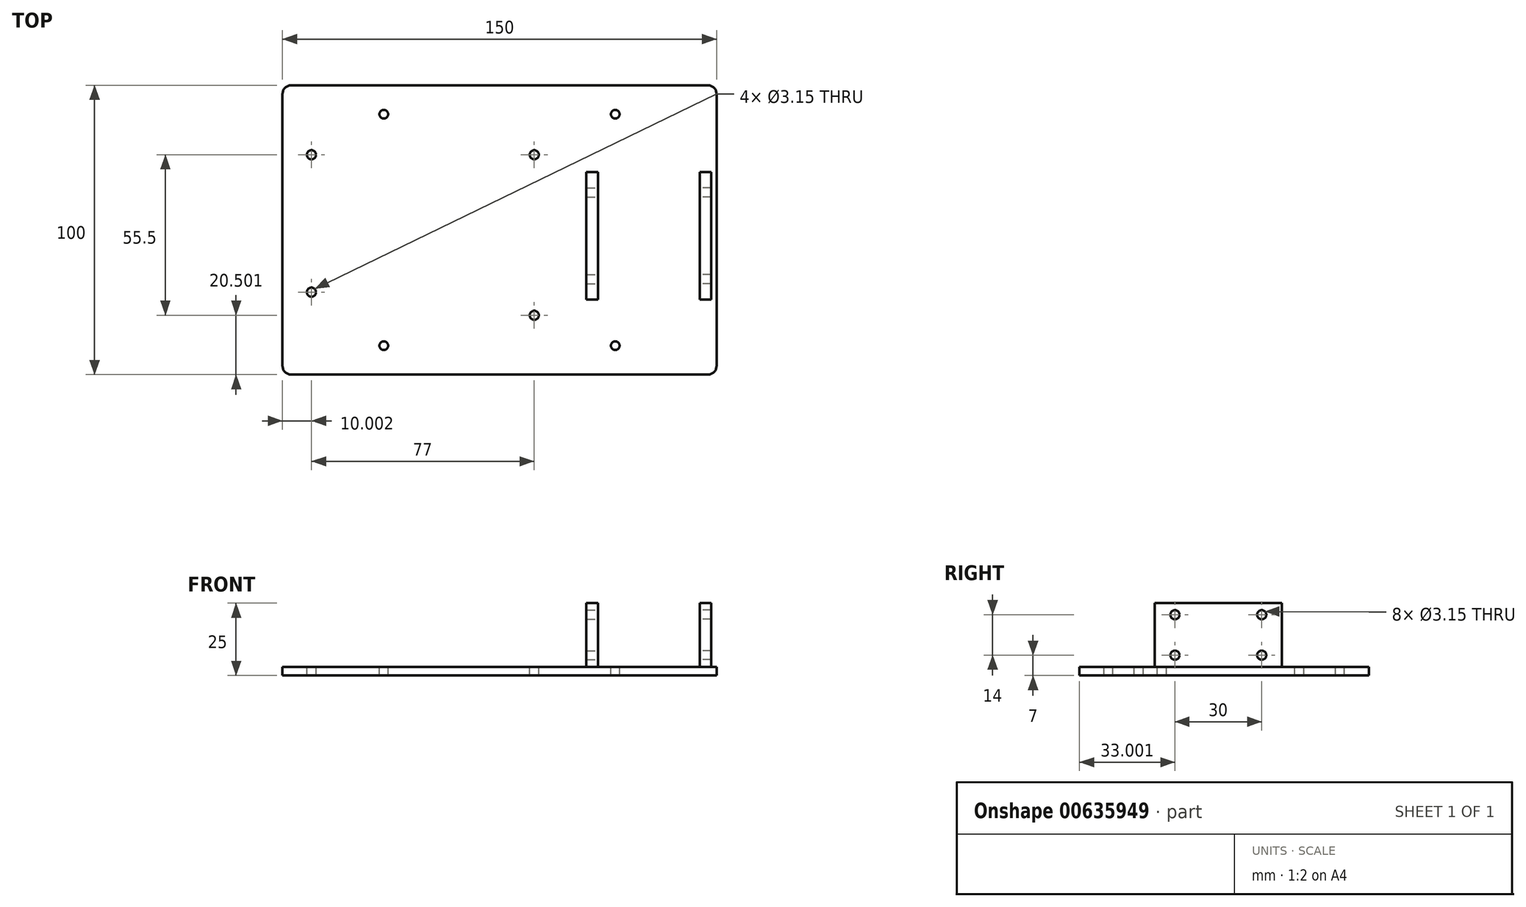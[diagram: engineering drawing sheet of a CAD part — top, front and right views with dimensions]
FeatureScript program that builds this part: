
annotation { "Feature Type Name" : "Feature", "Feature Type Description" : "" }
export const myFeature = defineFeature(function(context is Context, id is Id, definition is map)
    precondition{}
    {
        {
            var Q0;
            Q0=qCreatedBy(makeId("Top.planeOp"),FACE);
            var sketch = newSketch(context, id + "F0", { "sketchPlane" : qUnion([Q0])});
            skLineSegment(sketch, "E0.bottom", {"start": v(-81.67, 60.68) * mm, "end": v(68.33, 60.68) * mm});
            skLineSegment(sketch, "E0.top", {"start": v(-81.67, -39.32) * mm, "end": v(68.33, -39.32) * mm});
            skLineSegment(sketch, "E0.left", {"start": v(-81.67, 60.68) * mm, "end": v(-81.67, -39.32) * mm});
            skLineSegment(sketch, "E0.right", {"start": v(68.33, 60.68) * mm, "end": v(68.33, -39.32) * mm});
            skCircle(sketch, "E1", {"center": v(-46.67, 50.68) * mm, "radius": 1.5 * mm});
            skCircle(sketch, "E2", {"center": v(33.33, 50.68) * mm, "radius": 1.5 * mm});
            skCircle(sketch, "E3", {"center": v(33.33, -29.32) * mm, "radius": 1.5 * mm});
            skCircle(sketch, "E4", {"center": v(-46.67, -29.32) * mm, "radius": 1.5 * mm});
            skSolve(sketch);
        }
        {
            var Q0;
            Q0=makeQuery(id+"F0.imprint","IMPRINT",FACE,{"disambiguationData":[TD([[makeQuery(id+"F0.imprint","IMPRINT",EDGE,{"derivedFrom":sQuery(id+"F0.wireOp",EDGE,"E0.bottom")}),-1.0]])]});
            var sketch = newSketch(context, id + "F1", { "sketchPlane" : qUnion([Q0])});
            skCircle(sketch, "E5", {"center": v(-71.67, -10.82) * mm, "radius": 2 * mm});
            skCircle(sketch, "E6", {"center": v(-71.67, -10.82) * mm, "radius": 1 * mm});
            skCircle(sketch, "E7", {"center": v(-71.67, 36.68) * mm, "radius": 2 * mm});
            skCircle(sketch, "E8", {"center": v(-71.67, 36.68) * mm, "radius": 1 * mm});
            skCircle(sketch, "E9", {"center": v(5.33, -18.82) * mm, "radius": 2 * mm});
            skCircle(sketch, "E10", {"center": v(5.33, -18.82) * mm, "radius": 1 * mm});
            skCircle(sketch, "E11", {"center": v(5.33, 36.68) * mm, "radius": 2 * mm});
            skCircle(sketch, "E12", {"center": v(5.33, 36.68) * mm, "radius": 1 * mm});
            skLineSegment(sketch, "E13.bottom", {"start": v(23.33, 30.68) * mm, "end": v(27.33, 30.68) * mm});
            skLineSegment(sketch, "E13.top", {"start": v(23.33, -13.32) * mm, "end": v(27.33, -13.32) * mm});
            skLineSegment(sketch, "E13.left", {"start": v(23.33, 30.68) * mm, "end": v(23.33, -13.32) * mm});
            skLineSegment(sketch, "E13.right", {"start": v(27.33, 30.68) * mm, "end": v(27.33, -13.32) * mm});
            skLineSegment(sketch, "E14.bottom", {"start": v(62.53, 30.68) * mm, "end": v(66.53, 30.68) * mm});
            skLineSegment(sketch, "E14.top", {"start": v(62.53, -13.32) * mm, "end": v(66.53, -13.32) * mm});
            skLineSegment(sketch, "E14.left", {"start": v(62.53, 30.68) * mm, "end": v(62.53, -13.32) * mm});
            skLineSegment(sketch, "E14.right", {"start": v(66.53, 30.68) * mm, "end": v(66.53, -13.32) * mm});
            skSolve(sketch);
        }
        {
            var Q0;
            Q0=makeQuery(id+"F1.imprint","IMPRINT",FACE,{"disambiguationData":[TD([[makeQuery(id+"F1.imprint","IMPRINT",EDGE,{"derivedFrom":sQuery(id+"F1.wireOp",EDGE,"E13.bottom")}),-1.0]])]});
            var Q1;
            Q1=makeQuery(id+"F1.imprint","IMPRINT",FACE,{"disambiguationData":[TD([[makeQuery(id+"F1.imprint","IMPRINT",EDGE,{"derivedFrom":sQuery(id+"F1.wireOp",EDGE,"E14.bottom")}),-1.0]])]});
            extrude(context, id + "F2", {"entities" : qUnion([Q0, Q1]), "depth" : 22 * mm, "offsetDistance" : 25 * mm});
        }
        {
            var Q0;
            Q0=makeQuery(id+"F0.imprint","IMPRINT",FACE,{"disambiguationData":[TD([[makeQuery(id+"F0.imprint","IMPRINT",EDGE,{"derivedFrom":sQuery(id+"F0.wireOp",EDGE,"E0.bottom")}),-1.0]])]});
            extrude(context, id + "F3", {"entities" : qUnion([Q0]), "oppositeDirection" : true, "depth" : 3 * mm, "offsetDistance" : 25 * mm});
        }
        {
            var Q0;
            Q0=sQuery(id+"F1.wireOp",VERTEX,"E7.center");
            var Q1;
            Q1=makeQuery(id+"F3.opExtrude","SWEPT_BODY",BODY,{"disambiguationData":[OSD([sQuery(id+"F0.wireOp",EDGE,"E0.bottom"),sQuery(id+"F0.wireOp",EDGE,"E0.top"),sQuery(id+"F0.wireOp",EDGE,"E0.left"),sQuery(id+"F0.wireOp",EDGE,"E0.right")])]});
            hole(context, id + "F4", {"style" : HoleStyle.SIMPLE, "endStyle" : HoleEndStyle.THROUGH, "holeDiameter" : 3.15 * mm, "majorDiameter" : 5 * mm, "isTappedThrough" : true, "tappedDepth" : 12 * mm, "tapClearance" : 3, "locations" : qUnion([Q0]), "scope" : qUnion([Q1])});
        }
        {
            var Q0;
            Q0=sQuery(id+"F1.wireOp",VERTEX,"E11.center");
            var Q1;
            Q1=makeQuery(id+"F3.opExtrude","SWEPT_BODY",BODY,{"disambiguationData":[OSD([sQuery(id+"F0.wireOp",EDGE,"E0.bottom"),sQuery(id+"F0.wireOp",EDGE,"E0.top"),sQuery(id+"F0.wireOp",EDGE,"E0.left"),sQuery(id+"F0.wireOp",EDGE,"E0.right")])]});
            hole(context, id + "F5", {"style" : HoleStyle.SIMPLE, "endStyle" : HoleEndStyle.THROUGH, "holeDiameter" : 3.15 * mm, "majorDiameter" : 5 * mm, "isTappedThrough" : true, "tappedDepth" : 12 * mm, "tapClearance" : 3, "locations" : qUnion([Q0]), "scope" : qUnion([Q1])});
        }
        {
            var Q0;
            Q0=sQuery(id+"F1.wireOp",VERTEX,"E5.center");
            var Q1;
            Q1=makeQuery(id+"F3.opExtrude","SWEPT_BODY",BODY,{"disambiguationData":[OSD([sQuery(id+"F0.wireOp",EDGE,"E0.bottom"),sQuery(id+"F0.wireOp",EDGE,"E0.top"),sQuery(id+"F0.wireOp",EDGE,"E0.left"),sQuery(id+"F0.wireOp",EDGE,"E0.right")])]});
            hole(context, id + "F6", {"style" : HoleStyle.SIMPLE, "endStyle" : HoleEndStyle.THROUGH, "holeDiameter" : 3.15 * mm, "majorDiameter" : 5 * mm, "isTappedThrough" : true, "tappedDepth" : 12 * mm, "tapClearance" : 3, "locations" : qUnion([Q0]), "scope" : qUnion([Q1])});
        }
        {
            var Q0;
            Q0=sQuery(id+"F1.wireOp",VERTEX,"E9.center");
            var Q1;
            Q1=makeQuery(id+"F3.opExtrude","SWEPT_BODY",BODY,{"disambiguationData":[OSD([sQuery(id+"F0.wireOp",EDGE,"E0.bottom"),sQuery(id+"F0.wireOp",EDGE,"E0.top"),sQuery(id+"F0.wireOp",EDGE,"E0.left"),sQuery(id+"F0.wireOp",EDGE,"E0.right")])]});
            hole(context, id + "F7", {"style" : HoleStyle.SIMPLE, "endStyle" : HoleEndStyle.THROUGH, "holeDiameter" : 3.15 * mm, "majorDiameter" : 5 * mm, "isTappedThrough" : true, "tappedDepth" : 12 * mm, "tapClearance" : 3, "locations" : qUnion([Q0]), "scope" : qUnion([Q1])});
        }
        {
            var Q0;
            Q0=makeQuery(id+"F2.opExtrude","SWEPT_FACE",FACE,{"disambiguationData":[OSD([sQuery(id+"F1.wireOp",EDGE,"E13.right")])]});
            var sketch = newSketch(context, id + "F8", { "sketchPlane" : qUnion([Q0])});
            skCircle(sketch, "E15", {"center": v(-6.32, 18) * mm, "radius": 1.5 * mm});
            skCircle(sketch, "E16", {"center": v(23.68, 18) * mm, "radius": 1.5 * mm});
            skCircle(sketch, "E17", {"center": v(23.68, 4) * mm, "radius": 1.5 * mm});
            skCircle(sketch, "E18", {"center": v(-6.32, 4) * mm, "radius": 1.5 * mm});
            skSolve(sketch);
        }
        {
            var Q0;
            Q0=sQuery(id+"F8.wireOp",VERTEX,"E16.center");
            var Q1;
            Q1=sQuery(id+"F8.wireOp",VERTEX,"E17.center");
            var Q2;
            Q2=sQuery(id+"F8.wireOp",VERTEX,"E15.center");
            var Q3;
            Q3=sQuery(id+"F8.wireOp",VERTEX,"E18.center");
            var Q4;
            Q4=makeQuery(id+"F2.opExtrude","SWEPT_BODY",BODY,{"disambiguationData":[OSD([sQuery(id+"F1.wireOp",EDGE,"E13.bottom"),sQuery(id+"F1.wireOp",EDGE,"E13.top"),sQuery(id+"F1.wireOp",EDGE,"E13.left"),sQuery(id+"F1.wireOp",EDGE,"E13.right")])]});
            var Q5;
            Q5=makeQuery(id+"F2.opExtrude","SWEPT_BODY",BODY,{"disambiguationData":[OSD([sQuery(id+"F1.wireOp",EDGE,"E14.bottom"),sQuery(id+"F1.wireOp",EDGE,"E14.top"),sQuery(id+"F1.wireOp",EDGE,"E14.left"),sQuery(id+"F1.wireOp",EDGE,"E14.right")])]});
            hole(context, id + "F9", {"style" : HoleStyle.SIMPLE, "endStyle" : HoleEndStyle.THROUGH, "oppositeDirection" : true, "holeDiameter" : 3.15 * mm, "majorDiameter" : 5 * mm, "isTappedThrough" : true, "tappedDepth" : 12 * mm, "tapClearance" : 3, "locations" : qUnion([Q0, Q1, Q2, Q3]), "scope" : qUnion([Q4, Q5])});
        }
        {
            var Q0;
            Q0=makeQuery(id+"F3.opExtrude","SWEPT_EDGE",EDGE,{"disambiguationData":[OSD([sQuery(id+"F0.wireOp",EDGE,"E0.bottom"),sQuery(id+"F0.wireOp",EDGE,"E0.left")])]});
            fillet(context, id + "F10", {"entities" : qUnion([Q0]), "radius" : 3 * mm, "tangentPropagation" : true, "allowEdgeOverflow" : false});
        }
        {
            var Q0;
            Q0=makeQuery(id+"F3.opExtrude","SWEPT_EDGE",EDGE,{"disambiguationData":[OSD([sQuery(id+"F0.wireOp",EDGE,"E0.top"),sQuery(id+"F0.wireOp",EDGE,"E0.left")])]});
            var Q1;
            Q1=makeQuery(id+"F3.opExtrude","SWEPT_EDGE",EDGE,{"disambiguationData":[OSD([sQuery(id+"F0.wireOp",EDGE,"E0.top"),sQuery(id+"F0.wireOp",EDGE,"E0.right")])]});
            var Q2;
            Q2=makeQuery(id+"F3.opExtrude","SWEPT_EDGE",EDGE,{"disambiguationData":[OSD([sQuery(id+"F0.wireOp",EDGE,"E0.bottom"),sQuery(id+"F0.wireOp",EDGE,"E0.right")])]});
            fillet(context, id + "F11", {"entities" : qUnion([Q0, Q1, Q2]), "radius" : 3 * mm, "tangentPropagation" : true, "allowEdgeOverflow" : false});
        }
        {
            var Q0;
            Q0=sQuery(id+"F8.wireOp",VERTEX,"E16.center");
            var Q1;
            Q1=sQuery(id+"F8.wireOp",VERTEX,"E17.center");
            var Q2;
            Q2=sQuery(id+"F8.wireOp",VERTEX,"E18.center");
            var Q3;
            Q3=sQuery(id+"F8.wireOp",VERTEX,"E15.center");
            var Q4;
            Q4=makeQuery(id+"F2.opExtrude","SWEPT_BODY",BODY,{"disambiguationData":[OSD([sQuery(id+"F1.wireOp",EDGE,"E13.bottom"),sQuery(id+"F1.wireOp",EDGE,"E13.top"),sQuery(id+"F1.wireOp",EDGE,"E13.left"),sQuery(id+"F1.wireOp",EDGE,"E13.right")])]});
            hole(context, id + "F12", {"style" : HoleStyle.SIMPLE, "endStyle" : HoleEndStyle.THROUGH, "holeDiameter" : 3.15 * mm, "majorDiameter" : 5 * mm, "isTappedThrough" : true, "tappedDepth" : 12 * mm, "tapClearance" : 3, "locations" : qUnion([Q0, Q1, Q2, Q3]), "scope" : qUnion([Q4])});
        }
    });
